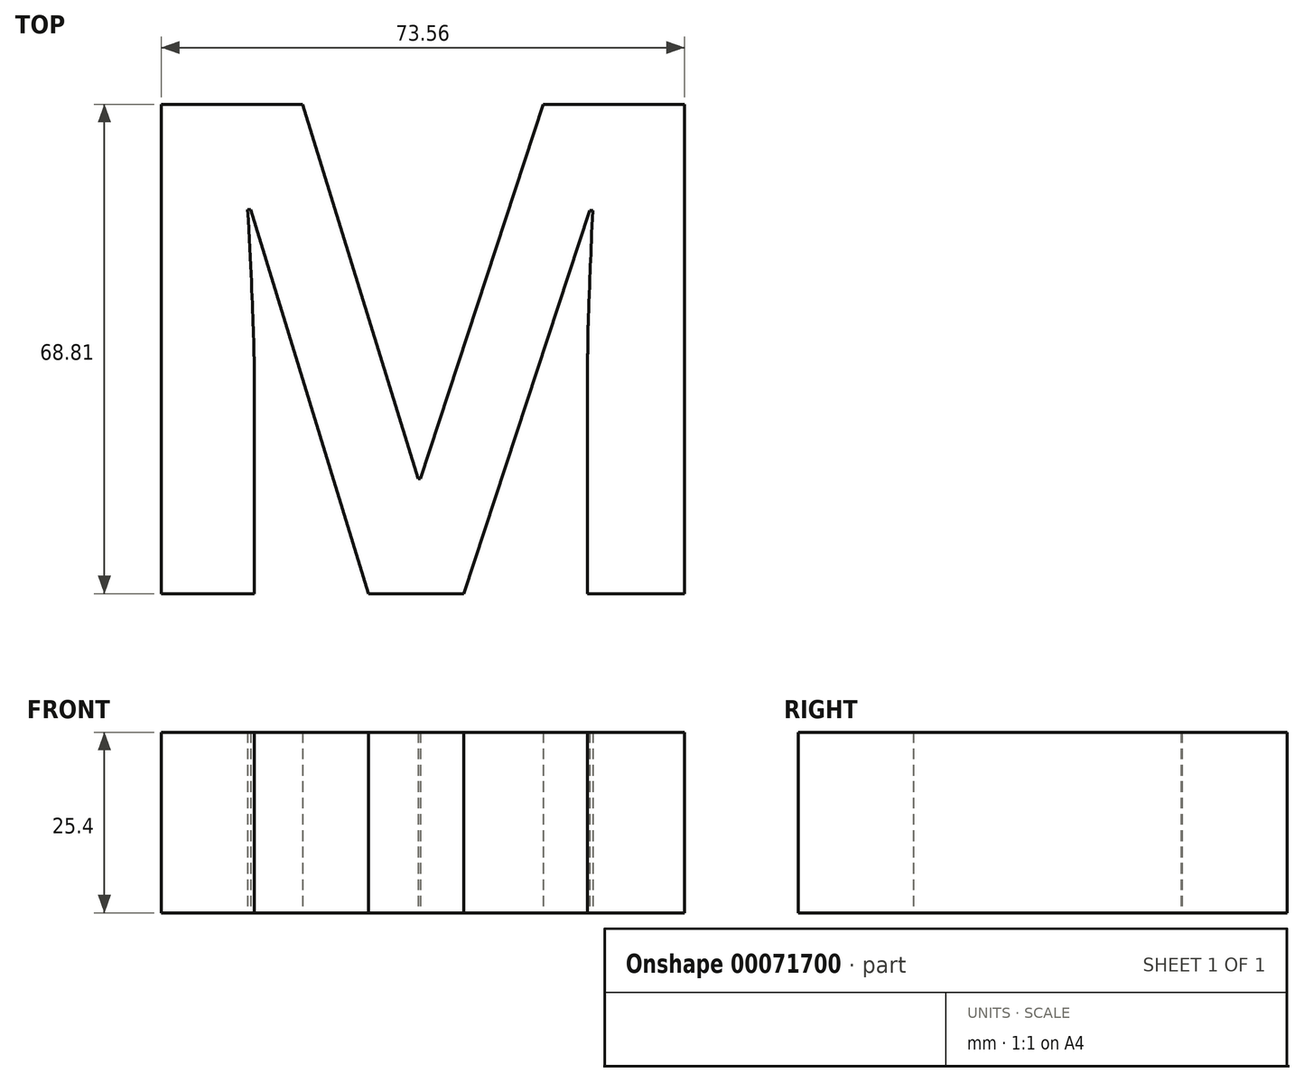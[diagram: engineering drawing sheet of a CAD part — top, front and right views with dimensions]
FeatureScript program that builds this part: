
annotation { "Feature Type Name" : "Feature", "Feature Type Description" : "" }
export const myFeature = defineFeature(function(context is Context, id is Id, definition is map)
    precondition{}
    {
        {
            var Q0;
            Q0=qCreatedBy(makeId("Top.planeOp"),FACE);
            var sketch = newSketch(context, id + "F0", { "sketchPlane" : qUnion([Q0])});
            skText(sketch, "E0", { "text": "M", "fontName": "NotoSans-Bold.ttf"});
            const initialGuessF0  = {"E0": [0, 0, 1, 0, 0.0694]};
            skSetInitialGuess(sketch, initialGuessF0);
            skSolve(sketch);
        }
        {
            var Q0;
            Q0 = qSketchRegion(id + "F0", true);
            extrude(context, id + "F1", {"entities" : qUnion([Q0]), "depth" : 25.4 * mm});
        }
    });
